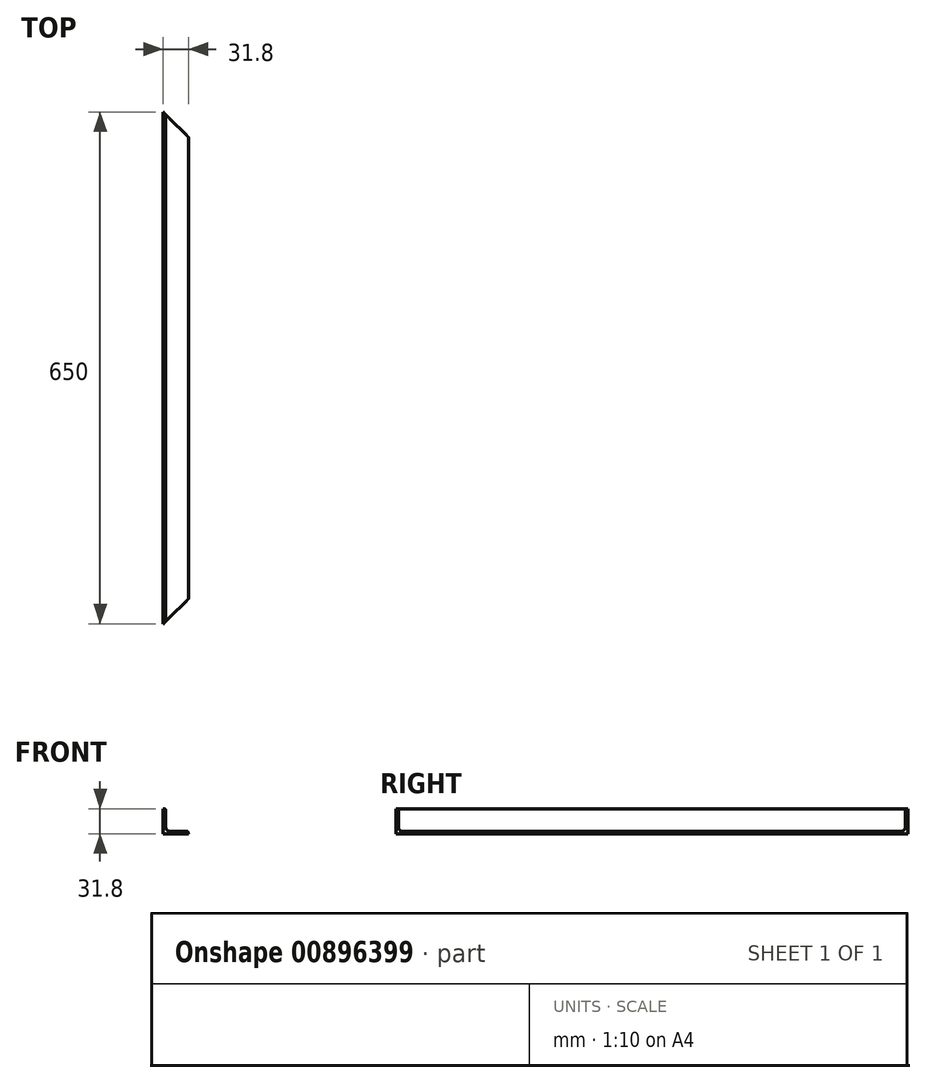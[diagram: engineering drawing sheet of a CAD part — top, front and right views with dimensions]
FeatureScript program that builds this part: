
annotation { "Feature Type Name" : "Feature", "Feature Type Description" : "" }
export const myFeature = defineFeature(function(context is Context, id is Id, definition is map)
    precondition{}
    {
        {
            var Q0;
            Q0=qCreatedBy(makeId("Front.planeOp"),FACE);
            var sketch = newSketch(context, id + "F0", { "sketchPlane" : qUnion([Q0])});
            skLineSegment(sketch, "E0", {"start": v(-10.15, 31.8) * mm, "end": v(-10.15, 0) * mm});
            skLineSegment(sketch, "E1", {"start": v(-10.15, 0) * mm, "end": v(21.65, 0) * mm});
            skLineSegment(sketch, "E2", {"start": v(21.65, 0) * mm, "end": v(21.65, 0.67) * mm});
            skLineSegment(sketch, "E3", {"start": v(19.15, 3.17) * mm, "end": v(-1.98, 3.17) * mm});
            skLineSegment(sketch, "E4", {"start": v(-6.98, 8.17) * mm, "end": v(-6.98, 29.3) * mm});
            skLineSegment(sketch, "E5", {"start": v(-9.48, 31.8) * mm, "end": v(-10.15, 31.8) * mm});
            skPoint(sketch, "E6.visualSharp", {"position": v(-6.98, 31.8) * mm});
            skArc(sketch, "E6.filletArc", {"start": v(-6.98, 29.3) * mm, "mid": v(-7.71, 31.07) * mm, "end": v(-9.48, 31.8) * mm});
            skPoint(sketch, "E7.visualSharp", {"position": v(21.65, 3.17) * mm});
            skArc(sketch, "E7.filletArc", {"start": v(21.65, 0.67) * mm, "mid": v(20.92, 2.44) * mm, "end": v(19.15, 3.17) * mm});
            skPoint(sketch, "E8.visualSharp", {"position": v(-6.98, 3.17) * mm});
            skArc(sketch, "E8.filletArc", {"start": v(-6.98, 8.17) * mm, "mid": v(-5.52, 4.63) * mm, "end": v(-1.98, 3.17) * mm});
            skSolve(sketch);
        }
        {
            var Q0;
            Q0=makeQuery(id+"F0.imprint","IMPRINT",FACE,{"disambiguationData":[TD([[makeQuery(id+"F0.imprint","IMPRINT",EDGE,{"derivedFrom":sQuery(id+"F0.wireOp",EDGE,"E0")}),1.0]])]});
            extrude(context, id + "F1", {"entities" : qUnion([Q0]), "depth" : 650 * mm, "offsetDistance" : 25 * mm});
        }
        {
            var Q0;
            Q0=makeQuery(id+"F1.opExtrude","SWEPT_FACE",FACE,{"disambiguationData":[OSD([sQuery(id+"F0.wireOp",EDGE,"E1")])]});
            var sketch = newSketch(context, id + "F2", { "sketchPlane" : qUnion([Q0])});
            skLineSegment(sketch, "E9", {"start": v(-10.15, 650) * mm, "end": v(21.65, 650) * mm});
            skLineSegment(sketch, "E10", {"start": v(21.65, 650) * mm, "end": v(21.65, 618.2) * mm});
            skLineSegment(sketch, "E11", {"start": v(21.65, 618.2) * mm, "end": v(-10.15, 650) * mm});
            skLineSegment(sketch, "E12", {"start": v(-10.15, 0) * mm, "end": v(21.65, 31.8) * mm});
            skLineSegment(sketch, "E13", {"start": v(21.65, 31.8) * mm, "end": v(21.65, 0) * mm});
            skLineSegment(sketch, "E14", {"start": v(21.65, 0) * mm, "end": v(-10.15, 0) * mm});
            skSolve(sketch);
        }
        {
            var Q0;
            Q0=makeQuery(id+"F2.imprint","IMPRINT",FACE,{"disambiguationData":[TD([[makeQuery(id+"F2.imprint","IMPRINT",EDGE,{"derivedFrom":sQuery(id+"F2.wireOp",EDGE,"E9")}),-1.0]])]});
            var Q1;
            Q1=makeQuery(id+"F2.imprint","IMPRINT",FACE,{"disambiguationData":[TD([[makeQuery(id+"F2.imprint","IMPRINT",EDGE,{"derivedFrom":sQuery(id+"F2.wireOp",EDGE,"E12")}),-1.0]])]});
            extrude(context, id + "F3", {"entities" : qUnion([Q0, Q1]), "operationType" : NewBodyOperationType.REMOVE, "oppositeDirection" : true, "depth" : 40 * mm, "offsetDistance" : 25 * mm});
        }
    });
